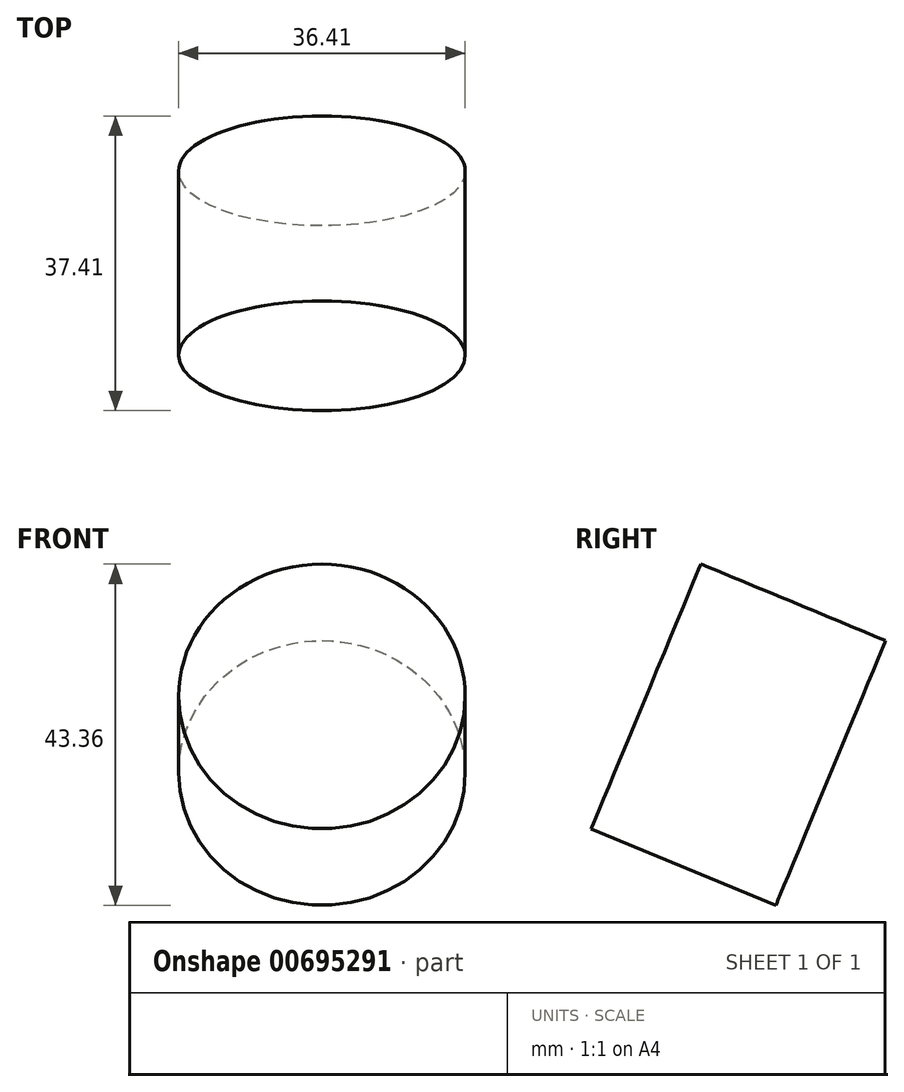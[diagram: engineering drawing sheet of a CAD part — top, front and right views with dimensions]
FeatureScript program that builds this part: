
annotation { "Feature Type Name" : "Feature", "Feature Type Description" : "" }
export const myFeature = defineFeature(function(context is Context, id is Id, definition is map)
    precondition{}
    {
        {
            var Q0;
            Q0=qCreatedBy(makeId("Front.planeOp"),FACE);
            var sketch = newSketch(context, id + "F0", { "sketchPlane" : qUnion([Q0])});
            skLineSegment(sketch, "E0", {"start": v(0, 203.2) * mm, "end": v(0, 0) * mm});
            skLineSegment(sketch, "E1.bottom", {"start": v(0, 203.2) * mm, "end": v(38.1, 203.2) * mm});
            skLineSegment(sketch, "E1.top", {"start": v(0, 165.1) * mm, "end": v(38.1, 165.1) * mm});
            skLineSegment(sketch, "E1.left", {"start": v(0, 203.2) * mm, "end": v(0, 165.1) * mm});
            skLineSegment(sketch, "E1.right", {"start": v(38.1, 203.2) * mm, "end": v(38.1, 165.1) * mm});
            skLineSegment(sketch, "E2", {"start": v(9.29, 165.1) * mm, "end": v(2.56, 0) * mm});
            skLineSegment(sketch, "E3", {"start": v(2.56, 0) * mm, "end": v(0, 0) * mm});
            skSolve(sketch);
        }
        {
            var Q0;
            Q0=qCreatedBy(makeId("Right.planeOp"),FACE);
            var sketch = newSketch(context, id + "F1", { "sketchPlane" : qUnion([Q0])});
            skLineSegment(sketch, "E4", {"start": v(-10.37, 175) * mm, "end": v(3.57, 169.22) * mm});
            skSolve(sketch);
        }
        {
            var Q0;
            Q0=sQuery(id+"F1.wireOp",EDGE,"E4");
            cPlane(context, id + "F2", {"entities" : qUnion([Q0]), "cplaneType" : CPlaneType.MID_PLANE, "offset" : 25.4 * mm, "width" : 152.4 * mm, "height" : 152.4 * mm});
        }
        {
            var Q0;
            Q0=qCreatedBy(makeId("Right.planeOp"),FACE);
            var sketch = newSketch(context, id + "F3", { "sketchPlane" : qUnion([Q0])});
            skLineSegment(sketch, "E5", {"start": v(34.86, 0) * mm, "end": v(34.86, 165.3) * mm});
            skLineSegment(sketch, "E6", {"start": v(34.86, 165.3) * mm, "end": v(51.54, 200.29) * mm});
            skLineSegment(sketch, "E7", {"start": v(51.54, 200.29) * mm, "end": v(45.97, 202.94) * mm});
            skLineSegment(sketch, "E8", {"start": v(45.97, 202.94) * mm, "end": v(21.12, 165.3) * mm});
            skLineSegment(sketch, "E9", {"start": v(21.12, 165.3) * mm, "end": v(33.4, 0) * mm});
            skLineSegment(sketch, "E10", {"start": v(33.4, 0) * mm, "end": v(34.86, 0) * mm});
            skSolve(sketch);
        }
        {
            var Q0;
            Q0=makeQuery(id+"F3.imprint","IMPRINT",FACE,{"disambiguationData":[TD([[makeQuery(id+"F3.imprint","IMPRINT",EDGE,{"derivedFrom":sQuery(id+"F3.wireOp",EDGE,"E5")}),1.0]])]});
            extrude(context, id + "F4", {"entities" : qUnion([Q0]), "endBound" : BoundingType.SYMMETRIC, "depth" : 63.5 * mm, "offsetDistance" : 25.4 * mm});
        }
        {
            var Q0;
            Q0=qCreatedBy(makeId("Front.planeOp"),FACE);
            var sketch = newSketch(context, id + "F5", { "sketchPlane" : qUnion([Q0])});
            skLineSegment(sketch, "E11", {"start": v(0, 0) * mm, "end": v(-2.47, 0) * mm});
            skLineSegment(sketch, "E12", {"start": v(-2.47, 0) * mm, "end": v(-9.28, 165.08) * mm});
            skLineSegment(sketch, "E13", {"start": v(-9.28, 165.08) * mm, "end": v(-36.76, 165.08) * mm});
            skLineSegment(sketch, "E14", {"start": v(-36.76, 165.08) * mm, "end": v(-36.76, 0) * mm});
            skLineSegment(sketch, "E15", {"start": v(-36.76, 0) * mm, "end": v(0, 0) * mm});
            skSolve(sketch);
        }
        {
            var Q0;
            {var subQ0=sQuery(id+"F5.wireOp",EDGE,"E12");Q0=makeQuery(id+"F5.imprint","IMPRINT",FACE,{"disambiguationData":[TD([[makeQuery(id+"F5.imprint","IMPRINT",EDGE,{"derivedFrom":subQ0}),1.0]])]});}
            extrude(context, id + "F6", {"entities" : qUnion([Q0]), "operationType" : NewBodyOperationType.REMOVE, "endBound" : BoundingType.SYMMETRIC, "oppositeDirection" : true, "depth" : 161.54 * mm, "offsetDistance" : 25.4 * mm});
        }
        {
            var Q0;
            Q0=qCreatedBy(makeId("Front.planeOp"),FACE);
            var sketch = newSketch(context, id + "F7", { "sketchPlane" : qUnion([Q0])});
            skLineSegment(sketch, "E16.bottom", {"start": v(115.05, -49.56) * mm, "end": v(0, -49.56) * mm});
            skLineSegment(sketch, "E16.top", {"start": v(115.05, 230.47) * mm, "end": v(0, 230.47) * mm});
            skLineSegment(sketch, "E16.left", {"start": v(115.05, -49.56) * mm, "end": v(115.05, 230.47) * mm});
            skLineSegment(sketch, "E16.right", {"start": v(0, -49.56) * mm, "end": v(0, 230.47) * mm});
            skSolve(sketch);
        }
        {
            var Q0;
            Q0=makeQuery(id+"F7.imprint","IMPRINT",FACE,{"disambiguationData":[TD([[makeQuery(id+"F7.imprint","IMPRINT",EDGE,{"derivedFrom":sQuery(id+"F7.wireOp",EDGE,"E16.bottom")}),-1.0]])]});
            extrude(context, id + "F8", {"entities" : qUnion([Q0]), "operationType" : NewBodyOperationType.REMOVE, "oppositeDirection" : true, "depth" : 80 * mm, "offsetDistance" : 25.4 * mm});
        }
        {
            var Q0;
            Q0=makeQuery(id+"F4.opExtrude","SWEPT_BODY",BODY,{"disambiguationData":[OSD([sQuery(id+"F3.wireOp",EDGE,"E5"),sQuery(id+"F3.wireOp",EDGE,"E6"),sQuery(id+"F3.wireOp",EDGE,"E7"),sQuery(id+"F3.wireOp",EDGE,"E8"),sQuery(id+"F3.wireOp",EDGE,"E9"),sQuery(id+"F3.wireOp",EDGE,"E10")])]});
            var Q1;
            Q1=makeQuery(id+"F8.boolean.opBoolean","COPY",FACE,{"derivedFrom":makeQuery(id+"F8.opExtrude","SWEPT_FACE",FACE,{"disambiguationData":[OSD([sQuery(id+"F7.wireOp",EDGE,"E16.right")])]})});
            mirror(context, id + "F9", {"operationType" : NewBodyOperationType.ADD, "entities" : qUnion([Q0]), "mirrorPlane" : qUnion([Q1])});
        }
        {
            var Q0;
            Q0=makeQuery(id+"F6.boolean.opBoolean","COPY",EDGE,{"derivedFrom":makeQuery(id+"F6.opExtrude","SWEPT_EDGE",EDGE,{"disambiguationData":[OSD([sQuery(id+"F5.wireOp",EDGE,"E12"),sQuery(id+"F5.wireOp",EDGE,"E13")])]})});
            var Q1;
            Q1=makeQuery(id+"F9.opPattern","COPY",EDGE,{"derivedFrom":makeQuery(id+"F6.boolean.opBoolean","COPY",EDGE,{"derivedFrom":makeQuery(id+"F6.opExtrude","SWEPT_EDGE",EDGE,{"disambiguationData":[OSD([sQuery(id+"F5.wireOp",EDGE,"E12"),sQuery(id+"F5.wireOp",EDGE,"E13")])]})}),"instanceName":"1"});
            var Q2;
            Q2=makeQuery(id+"F9.opPattern","COPY",EDGE,{"derivedFrom":makeQuery(id+"F6.boolean.opBoolean","INTERSECT",EDGE,{"derivedFrom":[makeQuery(id+"F4.opExtrude","CAP_FACE",FACE,{"disambiguationData":[OSD([sQuery(id+"F3.wireOp",EDGE,"E5"),sQuery(id+"F3.wireOp",EDGE,"E6"),sQuery(id+"F3.wireOp",EDGE,"E7"),sQuery(id+"F3.wireOp",EDGE,"E8"),sQuery(id+"F3.wireOp",EDGE,"E9"),sQuery(id+"F3.wireOp",EDGE,"E10")])],"isStart":true}),makeQuery(id+"F6.opExtrude","SWEPT_FACE",FACE,{"disambiguationData":[OSD([sQuery(id+"F5.wireOp",EDGE,"E13")])]})]}),"instanceName":"1"});
            var Q3;
            Q3=makeQuery(id+"F6.boolean.opBoolean","INTERSECT",EDGE,{"derivedFrom":[makeQuery(id+"F4.opExtrude","CAP_FACE",FACE,{"disambiguationData":[OSD([sQuery(id+"F3.wireOp",EDGE,"E5"),sQuery(id+"F3.wireOp",EDGE,"E6"),sQuery(id+"F3.wireOp",EDGE,"E7"),sQuery(id+"F3.wireOp",EDGE,"E8"),sQuery(id+"F3.wireOp",EDGE,"E9"),sQuery(id+"F3.wireOp",EDGE,"E10")])],"isStart":true}),makeQuery(id+"F6.opExtrude","SWEPT_FACE",FACE,{"disambiguationData":[OSD([sQuery(id+"F5.wireOp",EDGE,"E13")])]})]});
            fillet(context, id + "F10", {"entities" : qUnion([Q0, Q1, Q2, Q3]), "radius" : 5.08 * mm, "tangentPropagation" : true, "allowEdgeOverflow" : false});
        }
        {
            var Q0;
            Q0=makeQuery(id+"F4.opExtrude","CAP_EDGE",EDGE,{"disambiguationData":[OSD([sQuery(id+"F3.wireOp",EDGE,"E7")])],"isStart":true});
            var Q1;
            Q1=makeQuery(id+"F9.opPattern","COPY",EDGE,{"derivedFrom":makeQuery(id+"F4.opExtrude","CAP_EDGE",EDGE,{"disambiguationData":[OSD([sQuery(id+"F3.wireOp",EDGE,"E7")])],"isStart":true}),"instanceName":"1"});
            fillet(context, id + "F11", {"entities" : qUnion([Q0, Q1]), "radius" : 5.08 * mm, "tangentPropagation" : true, "allowEdgeOverflow" : false});
        }
        {
            var Q0;
            Q0=makeQuery(id+"F4.opExtrude","CAP_EDGE",EDGE,{"disambiguationData":[OSD([sQuery(id+"F3.wireOp",EDGE,"E8")])],"isStart":true});
            fillet(context, id + "F12", {"entities" : qUnion([Q0]), "radius" : 1.27 * mm, "tangentPropagation" : true, "allowEdgeOverflow" : false});
        }
        {
            var Q0;
            Q0=makeQuery(id+"F9.opPattern","COPY",EDGE,{"derivedFrom":makeQuery(id+"F6.boolean.opBoolean","INTERSECT",EDGE,{"derivedFrom":[makeQuery(id+"F4.opExtrude","SWEPT_FACE",FACE,{"disambiguationData":[OSD([sQuery(id+"F3.wireOp",EDGE,"E5")])]}),makeQuery(id+"F6.opExtrude","SWEPT_FACE",FACE,{"disambiguationData":[OSD([sQuery(id+"F5.wireOp",EDGE,"E12")])]})]}),"instanceName":"1"});
            var Q1;
            Q1=makeQuery(id+"F6.boolean.opBoolean","INTERSECT",EDGE,{"derivedFrom":[makeQuery(id+"F4.opExtrude","SWEPT_FACE",FACE,{"disambiguationData":[OSD([sQuery(id+"F3.wireOp",EDGE,"E5")])]}),makeQuery(id+"F6.opExtrude","SWEPT_FACE",FACE,{"disambiguationData":[OSD([sQuery(id+"F5.wireOp",EDGE,"E12")])]})]});
            fillet(context, id + "F13", {"entities" : qUnion([Q0, Q1]), "radius" : 5.08 * mm, "tangentPropagation" : true, "allowEdgeOverflow" : false});
        }
        {
            var Q0;
            {var subQ0=makeQuery(id+"F4.opExtrude","SWEPT_FACE",FACE,{"disambiguationData":[OSD([sQuery(id+"F3.wireOp",EDGE,"E9")])]});Q0=makeQuery(id+"F13.opFillet","BLEND_EDGE",EDGE,{"blendedFrom":[makeQuery(id+"F6.boolean.opBoolean","INTERSECT",EDGE,{"derivedFrom":[makeQuery(id+"F4.opExtrude","SWEPT_FACE",FACE,{"disambiguationData":[OSD([sQuery(id+"F3.wireOp",EDGE,"E5")])]}),makeQuery(id+"F6.opExtrude","SWEPT_FACE",FACE,{"disambiguationData":[OSD([sQuery(id+"F5.wireOp",EDGE,"E12")])]})]}),makeQuery(id+"F9.boolean.opBoolean","MERGE",FACE,{"derivedFrom":[subQ0,makeQuery(id+"F9.opPattern","COPY",FACE,{"derivedFrom":subQ0,"instanceName":"1"})]})],"blendedInto":[makeQuery(id+"F9.boolean.opBoolean","MERGE",FACE,{"derivedFrom":[subQ0,makeQuery(id+"F9.opPattern","COPY",FACE,{"derivedFrom":subQ0,"instanceName":"1"})]})]});}
            fillet(context, id + "F14", {"entities" : qUnion([Q0]), "radius" : 1.27 * mm, "tangentPropagation" : true, "allowEdgeOverflow" : false});
        }
        {
            var Q0;
            Q0=qCreatedBy(id+"F2.planeOp",FACE);
            var sketch = newSketch(context, id + "F15", { "sketchPlane" : qUnion([Q0])});
            skCircle(sketch, "E17", {"center": v(43.89, 157.86) * mm, "radius": 30.98 * mm});
            skCircle(sketch, "E18", {"center": v(12.94, 159.35) * mm, "radius": 28.41 * mm});
            skCircle(sketch, "E19", {"center": v(-38.68, 154.14) * mm, "radius": 18.2 * mm});
            skSolve(sketch);
        }
        {
            var Q0;
            Q0=makeQuery(id+"F15.imprint","IMPRINT",FACE,{"disambiguationData":[TD([[makeQuery(id+"F15.imprint","IMPRINT",EDGE,{"derivedFrom":sQuery(id+"F15.wireOp",EDGE,"E19")}),1.0]])]});
            extrude(context, id + "F16", {"entities" : qUnion([Q0]), "depth" : 25.4 * mm, "offsetDistance" : 25.4 * mm});
        }
        {
            var Q0;
            Q0=makeQuery(id+"F4.opExtrude","SWEPT_BODY",BODY,{"disambiguationData":[OSD([sQuery(id+"F3.wireOp",EDGE,"E5"),sQuery(id+"F3.wireOp",EDGE,"E6"),sQuery(id+"F3.wireOp",EDGE,"E7"),sQuery(id+"F3.wireOp",EDGE,"E8"),sQuery(id+"F3.wireOp",EDGE,"E9"),sQuery(id+"F3.wireOp",EDGE,"E10")])]});
            deleteBodies(context, id + "F17", {"entities" : qUnion([Q0])});
        }
    });
